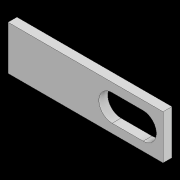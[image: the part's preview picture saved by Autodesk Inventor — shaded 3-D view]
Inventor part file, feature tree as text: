
AUTODESK INVENTOR PART (.ipt)
format: ipt  version: 2021 (Build 250183000, 183)  size: 88,576 bytes
history: native  units: in
note: dims shown in document units (in); Inventor stores cm internally (conversion verified against a paired STEP export)
features: extrude x1, sketch x1
ambient origin geometry x8: Origin, YZ Plane, XZ Plane, XY Plane, X Axis, Y Axis, Z Axis, Center Point
bodies: Solid1 (feature_tree)
feature tree (2):
  extrude  "Extrusion1"  Depth=1.378in
  sketch  "Sketch1"  dims[d0=0.3937in d1=1.378in d2=0.1181in d3=0.315in d4=0.2756in d5=0.0787in d6=0.0in]
